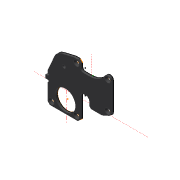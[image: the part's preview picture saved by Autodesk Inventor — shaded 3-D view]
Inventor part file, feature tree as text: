
AUTODESK INVENTOR PART (.ipt)
format: ipt  version: 2019.4 (Build 234330000, 330)  size: 183,808 bytes
history: native  units: mm
features: other x10, reference x5, sketch x2, hole x2, extrude x1, chamfer x1
ambient origin geometry x8: Origin, YZ Plane, XZ Plane, XY Plane, X Axis, Y Axis, Z Axis, Center Point
bodies: Body1 (feature_tree)
feature tree (21):
  other  "ソリッド1"
  sketch  "スケッチ1"
  extrude  "押し出し1"  Depth=3.0mm
  hole  "穴2"  [1 undecoded]
  hole  "穴3"  [1 undecoded]
  chamfer  "面取り1"  Distance=0.25mm
  reference  "参照1"
  reference  "参照2"
  reference  "参照3"
  reference  "参照4"
  sketch  "スケッチ2"
  reference  "参照5"
  parser-record x2  (decoder bookkeeping rows leaked as tree rows — omitted from the tree; the rows remain in map.json)
  other  "COXA_YAW_BLOCK_ASM2.iam"
  other  "COXA_YAW_ROLL_ADPT_SPACER:1"
  other  "COXA_UNIT_ASM.iam"
  other  "XM430_ASM_WITHOUT-BACK:2"
  other  "XM430_HOUSING_MIDDLE:1"
  other  "XM430_ASM_WITHOUT-BACK:1"
  other  "XM430_HOUSING_TOP:1"
note: 2 required parameter values undecoded (feature->parameter linkage not recoverable at this tier; creation-order binding heuristic only, values carry confidence <= 0.55)
note: 2 file-system paths scrubbed to <path> (originals preserved in map.json)
